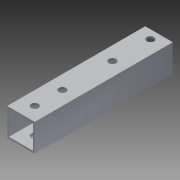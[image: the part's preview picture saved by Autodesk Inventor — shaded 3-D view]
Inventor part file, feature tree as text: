
AUTODESK INVENTOR PART (.ipt)
format: ipt  version: 2014 (Build 180170000, 170)  size: 102,912 bytes
history: native  units: in
note: dims shown in document units (in); Inventor stores cm internally (conversion verified against a paired STEP export)
features: extrude x2, sketch x2
ambient origin geometry x8: Origin, YZ Plane, XZ Plane, XY Plane, X Axis, Y Axis, Z Axis, Center Point
bodies: Solid1 (feature_tree)
feature tree (4):
  extrude  "Extrusion1"  Depth=1.0in
  extrude  "Extrusion2"  Depth=5.0in TaperAngle=0.0deg
  sketch  "Sketch1"  dims[d0=1.0in d1=1.0in]
  sketch  "Sketch2"  dims[d2=0.0625in d3=5.0in d4=0.0in d5=0.266in d6=0.3125in d7=0.5in d8=0.7874in d10=1.375in d11=0.3937in d13=1.0in d15=4.0in d16=0.0in d17=0.5in d18=1.8125in d19=0.7874in d21=1.0in d22=0.3937in d24=1.0in]
